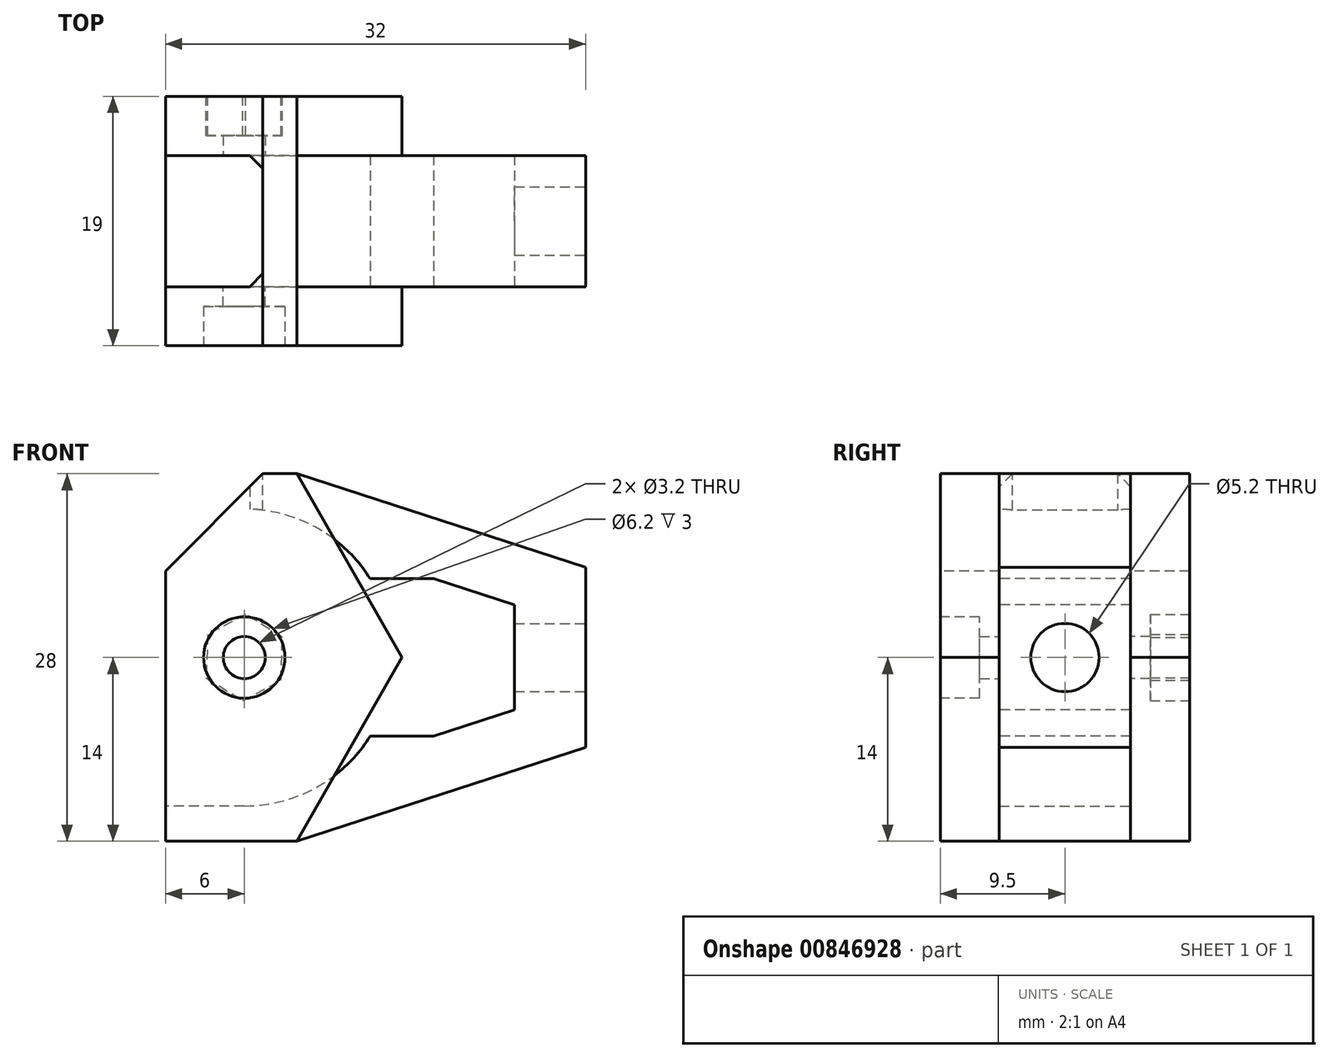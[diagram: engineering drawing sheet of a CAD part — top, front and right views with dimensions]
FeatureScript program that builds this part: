
annotation { "Feature Type Name" : "Feature", "Feature Type Description" : "" }
export const myFeature = defineFeature(function(context is Context, id is Id, definition is map)
    precondition{}
    {
        {
            var Q0;
            Q0=qCreatedBy(makeId("Front.planeOp"),FACE);
            var sketch = newSketch(context, id + "F0", { "sketchPlane" : qUnion([Q0])});
            skLineSegment(sketch, "E0.bottom", {"start": v(16, -14) * mm, "end": v(-16, -14) * mm});
            skLineSegment(sketch, "E0.top", {"start": v(16, 14) * mm, "end": v(-16, 14) * mm});
            skLineSegment(sketch, "E0.left", {"start": v(16, -14) * mm, "end": v(16, 14) * mm});
            skLineSegment(sketch, "E0.right", {"start": v(-16, -14) * mm, "end": v(-16, 14) * mm});
            skPoint(sketch, "E0.middle", {"position": v(0, 0) * mm});
            skPoint(sketch, "E1", {"position": v(-10, 0) * mm});
            skCircle(sketch, "E2", {"center": v(-10, 0) * mm, "radius": 1.6 * mm});
            skSolve(sketch);
        }
        {
            var Q0;
            Q0 = qSketchRegion(id + "F0", true);
            extrude(context, id + "F1", {"entities" : qUnion([Q0]), "depth" : 9.5 * mm, "offsetDistance" : 25 * mm});
        }
        {
            var Q0;
            Q0=makeQuery(id+"F1.opExtrude","CAP_FACE",FACE,{"disambiguationData":[OSD([sQuery(id+"F0.wireOp",EDGE,"E0.bottom"),sQuery(id+"F0.wireOp",EDGE,"E0.top"),sQuery(id+"F0.wireOp",EDGE,"E0.left"),sQuery(id+"F0.wireOp",EDGE,"E0.right"),sQuery(id+"F0.wireOp",EDGE,"E2")])],"isStart":false});
            var sketch = newSketch(context, id + "F2", { "sketchPlane" : qUnion([Q0])});
            skLineSegment(sketch, "E3", {"start": v(16, 14) * mm, "end": v(-6, 14) * mm});
            skLineSegment(sketch, "E4", {"start": v(-6, 14) * mm, "end": v(2, 0) * mm});
            skLineSegment(sketch, "E5", {"start": v(2, 0) * mm, "end": v(-6, -14) * mm});
            skLineSegment(sketch, "E6", {"start": v(-6, -14) * mm, "end": v(16, -14) * mm});
            skLineSegment(sketch, "E7", {"start": v(16, -14) * mm, "end": v(16, 14) * mm});
            skSolve(sketch);
        }
        {
            var Q0;
            Q0 = qSketchRegion(id + "F2", true);
            extrude(context, id + "F3", {"entities" : qUnion([Q0]), "operationType" : NewBodyOperationType.REMOVE, "oppositeDirection" : true, "depth" : 4.5 * mm, "offsetDistance" : 25 * mm});
        }
        {
            var Q0;
            Q0=makeQuery(id+"F3.boolean.opBoolean","COPY",FACE,{"derivedFrom":makeQuery(id+"F3.opExtrude","CAP_FACE",FACE,{"disambiguationData":[OSD([sQuery(id+"F2.wireOp",EDGE,"E3"),sQuery(id+"F2.wireOp",EDGE,"E4"),sQuery(id+"F2.wireOp",EDGE,"E5"),sQuery(id+"F2.wireOp",EDGE,"E6"),sQuery(id+"F2.wireOp",EDGE,"E7")])],"isStart":false})});
            var sketch = newSketch(context, id + "F4", { "sketchPlane" : qUnion([Q0])});
            skCircle(sketch, "E8.0", {"center": v(-10, 0) * mm, "radius": 1.6 * mm, "construction": true});
            skLineSegment(sketch, "E9", {"start": v(-0.4, 6) * mm, "end": v(10.6, 6) * mm});
            skLineSegment(sketch, "E10", {"start": v(10.6, 6) * mm, "end": v(10.6, -6) * mm});
            skLineSegment(sketch, "E11", {"start": v(10.6, -6) * mm, "end": v(-0.4, -6) * mm});
            skLineSegment(sketch, "E12", {"start": v(0, 0) * mm, "end": v(10.6, 0) * mm, "construction": true});
            skArc(sketch, "E13", {"start": v(-0.4, 6) * mm, "mid": v(-4.52, 9.9) * mm, "end": v(-10, 11.31) * mm});
            skPoint(sketch, "E14.start.orphan", {"position": v(-3.14, 9) * mm});
            skPoint(sketch, "E15.end.orphan", {"position": v(-3.14, -9) * mm});
            skLineSegment(sketch, "E16", {"start": v(-10, 11.31) * mm, "end": v(-20, 11.31) * mm});
            skLineSegment(sketch, "E17", {"start": v(-10, -11.31) * mm, "end": v(-20, -11.31) * mm});
            skArc(sketch, "E18.trimOffspring", {"start": v(-10, -11.31) * mm, "mid": v(-4.52, -9.9) * mm, "end": v(-0.4, -6) * mm});
            skLineSegment(sketch, "E19", {"start": v(-20, 11.31) * mm, "end": v(-20, -11.31) * mm});
            skSolve(sketch);
        }
        {
            var Q0;
            Q0 = qSketchRegion(id + "F4", true);
            var Q1;
            Q1=makeQuery(id+"F1.opExtrude","CAP_FACE",FACE,{"disambiguationData":[OSD([sQuery(id+"F0.wireOp",EDGE,"E0.bottom"),sQuery(id+"F0.wireOp",EDGE,"E0.top"),sQuery(id+"F0.wireOp",EDGE,"E0.left"),sQuery(id+"F0.wireOp",EDGE,"E0.right"),sQuery(id+"F0.wireOp",EDGE,"E2")])],"isStart":true});
            extrude(context, id + "F5", {"entities" : qUnion([Q0]), "operationType" : NewBodyOperationType.REMOVE, "endBound" : BoundingType.UP_TO_SURFACE, "oppositeDirection" : true, "depth" : 25 * mm, "endBoundEntityFace" : qUnion([Q1]), "offsetDistance" : 25 * mm});
        }
        {
            var Q0;
            Q0=makeQuery(id+"F5.boolean.opBoolean","COPY",FACE,{"derivedFrom":makeQuery(id+"F5.opExtrude","CAP_FACE",FACE,{"disambiguationData":[OSD([sQuery(id+"F4.wireOp",EDGE,"E9"),sQuery(id+"F4.wireOp",EDGE,"E10"),sQuery(id+"F4.wireOp",EDGE,"E11"),sQuery(id+"F4.wireOp",EDGE,"E13"),sQuery(id+"F4.wireOp",EDGE,"E16"),sQuery(id+"F4.wireOp",EDGE,"E17"),sQuery(id+"F4.wireOp",EDGE,"E18.trimOffspring"),sQuery(id+"F4.wireOp",EDGE,"E19")])],"isStart":true})});
            var sketch = newSketch(context, id + "F6", { "sketchPlane" : qUnion([Q0])});
            skLineSegment(sketch, "E20.0", {"start": v(-2, 0) * mm, "end": v(3.14, -9) * mm});
            skLineSegment(sketch, "E20.1", {"start": v(3.14, 9) * mm, "end": v(-2, 0) * mm});
            skArc(sketch, "E20.2", {"start": v(3.14, 9) * mm, "mid": v(6.38, 10.72) * mm, "end": v(10, 11.31) * mm});
            skLineSegment(sketch, "E20.3", {"start": v(10, 11.31) * mm, "end": v(16, 11.31) * mm});
            skLineSegment(sketch, "E20.4", {"start": v(16, 11.31) * mm, "end": v(16, -11.31) * mm});
            skLineSegment(sketch, "E20.5", {"start": v(10, -11.31) * mm, "end": v(16, -11.31) * mm});
            skArc(sketch, "E20.6", {"start": v(10, -11.31) * mm, "mid": v(6.38, -10.72) * mm, "end": v(3.14, -9) * mm});
            skSolve(sketch);
        }
        {
            var Q0;
            Q0=makeQuery(id+"F1.opExtrude","SWEPT_BODY",BODY,{"disambiguationData":[OSD([sQuery(id+"F0.wireOp",EDGE,"E0.bottom"),sQuery(id+"F0.wireOp",EDGE,"E0.top"),sQuery(id+"F0.wireOp",EDGE,"E0.left"),sQuery(id+"F0.wireOp",EDGE,"E0.right"),sQuery(id+"F0.wireOp",EDGE,"E2")])]});
            var Q1;
            Q1=qCreatedBy(makeId("Front.planeOp"),FACE);
            mirror(context, id + "F7", {"operationType" : NewBodyOperationType.ADD, "entities" : qUnion([Q0]), "mirrorPlane" : qUnion([Q1])});
        }
        {
            var Q0;
            {var subQ0=makeQuery(id+"F1.opExtrude","SWEPT_FACE",FACE,{"disambiguationData":[OSD([sQuery(id+"F0.wireOp",EDGE,"E0.left")])]});Q0=makeQuery(id+"F7.boolean.opBoolean","MERGE",FACE,{"derivedFrom":[subQ0,makeQuery(id+"F7.opPattern","COPY",FACE,{"derivedFrom":subQ0,"instanceName":"1"})]});}
            var sketch = newSketch(context, id + "F8", { "sketchPlane" : qUnion([Q0])});
            skCircle(sketch, "E21", {"center": v(0, 0) * mm, "radius": 2.6 * mm});
            skSolve(sketch);
        }
        {
            var Q0;
            Q0 = qSketchRegion(id + "F8", true);
            extrude(context, id + "F9", {"entities" : qUnion([Q0]), "operationType" : NewBodyOperationType.REMOVE, "oppositeDirection" : true, "depth" : 25 * mm, "offsetDistance" : 25 * mm});
        }
        {
            var Q0;
            Q0=makeQuery(id+"F7.opPattern","COPY",FACE,{"derivedFrom":makeQuery(id+"F1.opExtrude","CAP_FACE",FACE,{"disambiguationData":[OSD([sQuery(id+"F0.wireOp",EDGE,"E0.bottom"),sQuery(id+"F0.wireOp",EDGE,"E0.top"),sQuery(id+"F0.wireOp",EDGE,"E0.left"),sQuery(id+"F0.wireOp",EDGE,"E0.right"),sQuery(id+"F0.wireOp",EDGE,"E2")])],"isStart":false}),"instanceName":"1"});
            var sketch = newSketch(context, id + "F10", { "sketchPlane" : qUnion([Q0])});
            skCircle(sketch, "E22.0", {"center": v(10, 0) * mm, "radius": 1.6 * mm, "construction": true});
            skCircle(sketch, "E23.cCircle", {"center": v(10, 0) * mm, "radius": 2.85 * mm, "construction": true});
            skLineSegment(sketch, "E23.0", {"start": v(12.9, -1.54) * mm, "end": v(10.12, -3.29) * mm});
            skLineSegment(sketch, "E23.1", {"start": v(10.12, -3.29) * mm, "end": v(7.2, -1.74) * mm});
            skLineSegment(sketch, "E23.2", {"start": v(7.2, -1.74) * mm, "end": v(7.1, 1.54) * mm});
            skLineSegment(sketch, "E23.3", {"start": v(7.1, 1.54) * mm, "end": v(9.88, 3.29) * mm});
            skLineSegment(sketch, "E23.4", {"start": v(9.88, 3.29) * mm, "end": v(12.8, 1.74) * mm});
            skLineSegment(sketch, "E23.5", {"start": v(12.8, 1.74) * mm, "end": v(12.9, -1.54) * mm});
            skPoint(sketch, "E23.0.midPoint", {"position": v(11.51, -2.42) * mm});
            skSolve(sketch);
        }
        {
            var Q0;
            Q0 = qSketchRegion(id + "F10", true);
            extrude(context, id + "F11", {"entities" : qUnion([Q0]), "operationType" : NewBodyOperationType.REMOVE, "oppositeDirection" : true, "depth" : 3 * mm, "offsetDistance" : 25 * mm});
        }
        {
            var Q0;
            Q0=makeQuery(id+"F1.opExtrude","CAP_FACE",FACE,{"disambiguationData":[OSD([sQuery(id+"F0.wireOp",EDGE,"E0.bottom"),sQuery(id+"F0.wireOp",EDGE,"E0.top"),sQuery(id+"F0.wireOp",EDGE,"E0.left"),sQuery(id+"F0.wireOp",EDGE,"E0.right"),sQuery(id+"F0.wireOp",EDGE,"E2")])],"isStart":false});
            var sketch = newSketch(context, id + "F12", { "sketchPlane" : qUnion([Q0])});
            skCircle(sketch, "E24.0", {"center": v(-10, 0) * mm, "radius": 1.6 * mm, "construction": true});
            skCircle(sketch, "E25", {"center": v(-10, 0) * mm, "radius": 3.1 * mm});
            skSolve(sketch);
        }
        {
            var Q0;
            Q0 = qSketchRegion(id + "F12", true);
            extrude(context, id + "F13", {"entities" : qUnion([Q0]), "operationType" : NewBodyOperationType.REMOVE, "oppositeDirection" : true, "depth" : 3 * mm, "offsetDistance" : 25 * mm});
        }
        {
            var Q0;
            Q0=makeQuery(id+"F3.boolean.opBoolean","COPY",FACE,{"derivedFrom":makeQuery(id+"F3.opExtrude","CAP_FACE",FACE,{"disambiguationData":[OSD([sQuery(id+"F2.wireOp",EDGE,"E3"),sQuery(id+"F2.wireOp",EDGE,"E4"),sQuery(id+"F2.wireOp",EDGE,"E5"),sQuery(id+"F2.wireOp",EDGE,"E6"),sQuery(id+"F2.wireOp",EDGE,"E7")])],"isStart":false})});
            var sketch = newSketch(context, id + "F14", { "sketchPlane" : qUnion([Q0])});
            skLineSegment(sketch, "E26", {"start": v(16, 14) * mm, "end": v(16, 6.86) * mm});
            skLineSegment(sketch, "E27", {"start": v(-6, -14) * mm, "end": v(16, -6.86) * mm});
            skLineSegment(sketch, "E28", {"start": v(16, -6.86) * mm, "end": v(16, -14) * mm});
            skLineSegment(sketch, "E29", {"start": v(16, -14) * mm, "end": v(-6, -14) * mm});
            skLineSegment(sketch, "E30", {"start": v(16, 14) * mm, "end": v(-6, 14) * mm});
            skLineSegment(sketch, "E31", {"start": v(-6, 14) * mm, "end": v(16, 6.86) * mm});
            skPoint(sketch, "E32", {"position": v(16, 0) * mm});
            skSolve(sketch);
        }
        {
            var Q0;
            Q0 = qSketchRegion(id + "F14", true);
            extrude(context, id + "F15", {"entities" : qUnion([Q0]), "operationType" : NewBodyOperationType.REMOVE, "oppositeDirection" : true, "depth" : 25 * mm, "offsetDistance" : 25 * mm});
        }
        {
            var Q0;
            Q0=makeQuery(id+"F3.boolean.opBoolean","COPY",FACE,{"derivedFrom":makeQuery(id+"F3.opExtrude","CAP_FACE",FACE,{"disambiguationData":[OSD([sQuery(id+"F2.wireOp",EDGE,"E3"),sQuery(id+"F2.wireOp",EDGE,"E4"),sQuery(id+"F2.wireOp",EDGE,"E5"),sQuery(id+"F2.wireOp",EDGE,"E6"),sQuery(id+"F2.wireOp",EDGE,"E7")])],"isStart":false})});
            var sketch = newSketch(context, id + "F16", { "sketchPlane" : qUnion([Q0])});
            skLineSegment(sketch, "E33", {"start": v(4.43, 6) * mm, "end": v(10.6, 4) * mm});
            skLineSegment(sketch, "E34", {"start": v(10.6, 4) * mm, "end": v(10.6, 6) * mm});
            skLineSegment(sketch, "E35", {"start": v(10.6, 6) * mm, "end": v(4.43, 6) * mm});
            skLineSegment(sketch, "E36.MirrorCS", {"start": v(10.6, -6) * mm, "end": v(4.43, -6) * mm});
            skLineSegment(sketch, "E37.MirrorCS", {"start": v(4.43, -6) * mm, "end": v(10.6, -4) * mm});
            skLineSegment(sketch, "E38.MirrorCS", {"start": v(10.6, -4) * mm, "end": v(10.6, -6) * mm});
            skSolve(sketch);
        }
        {
            var Q0;
            Q0 = qSketchRegion(id + "F16", true);
            var Q1;
            Q1=makeQuery(id+"F7.opPattern","COPY",FACE,{"derivedFrom":makeQuery(id+"F3.boolean.opBoolean","COPY",FACE,{"derivedFrom":makeQuery(id+"F3.opExtrude","CAP_FACE",FACE,{"disambiguationData":[OSD([sQuery(id+"F2.wireOp",EDGE,"E3"),sQuery(id+"F2.wireOp",EDGE,"E4"),sQuery(id+"F2.wireOp",EDGE,"E5"),sQuery(id+"F2.wireOp",EDGE,"E6"),sQuery(id+"F2.wireOp",EDGE,"E7")])],"isStart":false})}),"instanceName":"1"});
            extrude(context, id + "F17", {"entities" : qUnion([Q0]), "operationType" : NewBodyOperationType.ADD, "endBound" : BoundingType.UP_TO_SURFACE, "oppositeDirection" : true, "depth" : 25 * mm, "endBoundEntityFace" : qUnion([Q1]), "offsetDistance" : 25 * mm});
        }
        {
            var Q0;
            {var subQ0=makeQuery(id+"F1.opExtrude","SWEPT_FACE",FACE,{"disambiguationData":[OSD([sQuery(id+"F0.wireOp",EDGE,"E0.top")])]});Q0=makeQuery(id+"F7.boolean.opBoolean","MERGE",FACE,{"derivedFrom":[subQ0,makeQuery(id+"F7.opPattern","COPY",FACE,{"derivedFrom":subQ0,"instanceName":"1"})]});}
            var sketch = newSketch(context, id + "F18", { "sketchPlane" : qUnion([Q0])});
            skPoint(sketch, "E39.0", {"position": v(-16, 5) * mm});
            skPoint(sketch, "E40.0", {"position": v(-16, -5) * mm});
            skLineSegment(sketch, "E41.bottom", {"start": v(-16, 5) * mm, "end": v(-8.58, 5) * mm});
            skLineSegment(sketch, "E41.top", {"start": v(-16, -5) * mm, "end": v(-8.58, -5) * mm});
            skLineSegment(sketch, "E41.left", {"start": v(-16, 5) * mm, "end": v(-16, -5) * mm});
            skLineSegment(sketch, "E41.right", {"start": v(-8.58, 5) * mm, "end": v(-8.58, -5) * mm});
            skSolve(sketch);
        }
        {
            var Q0;
            Q0 = qSketchRegion(id + "F18", true);
            extrude(context, id + "F19", {"entities" : qUnion([Q0]), "operationType" : NewBodyOperationType.REMOVE, "oppositeDirection" : true, "depth" : 5 * mm, "offsetDistance" : 25 * mm});
        }
        {
            var Q0;
            Q0=makeQuery(id+"F1.opExtrude","CAP_FACE",FACE,{"disambiguationData":[OSD([sQuery(id+"F0.wireOp",EDGE,"E0.bottom"),sQuery(id+"F0.wireOp",EDGE,"E0.top"),sQuery(id+"F0.wireOp",EDGE,"E0.left"),sQuery(id+"F0.wireOp",EDGE,"E0.right"),sQuery(id+"F0.wireOp",EDGE,"E2")])],"isStart":false});
            var sketch = newSketch(context, id + "F20", { "sketchPlane" : qUnion([Q0])});
            skPoint(sketch, "E42.0", {"position": v(-8.58, 14) * mm});
            skLineSegment(sketch, "E43", {"start": v(-8.58, 14) * mm, "end": v(-16, 6.58) * mm});
            skLineSegment(sketch, "E44", {"start": v(-16, 6.58) * mm, "end": v(-16, 14) * mm});
            skLineSegment(sketch, "E45", {"start": v(-16, 14) * mm, "end": v(-8.58, 14) * mm});
            skSolve(sketch);
        }
        {
            var Q0;
            Q0 = qSketchRegion(id + "F20", true);
            extrude(context, id + "F21", {"entities" : qUnion([Q0]), "operationType" : NewBodyOperationType.REMOVE, "oppositeDirection" : true, "depth" : 25 * mm, "offsetDistance" : 25 * mm});
        }
        {
            var Q0;
            Q0=makeQuery(id+"F19.boolean.opBoolean","COPY",EDGE,{"derivedFrom":makeQuery(id+"F19.opExtrude","SWEPT_EDGE",EDGE,{"disambiguationData":[OSD([sQuery(id+"F18.wireOp",EDGE,"E41.top"),sQuery(id+"F18.wireOp",EDGE,"E41.right")])]})});
            var Q1;
            Q1=makeQuery(id+"F19.boolean.opBoolean","COPY",EDGE,{"derivedFrom":makeQuery(id+"F19.opExtrude","SWEPT_EDGE",EDGE,{"disambiguationData":[OSD([sQuery(id+"F18.wireOp",EDGE,"E41.bottom"),sQuery(id+"F18.wireOp",EDGE,"E41.right")])]})});
            chamfer(context, id + "F22", {"entities" : qUnion([Q0, Q1]), "width" : 1 * mm, "tangentPropagation" : true});
        }
    });
